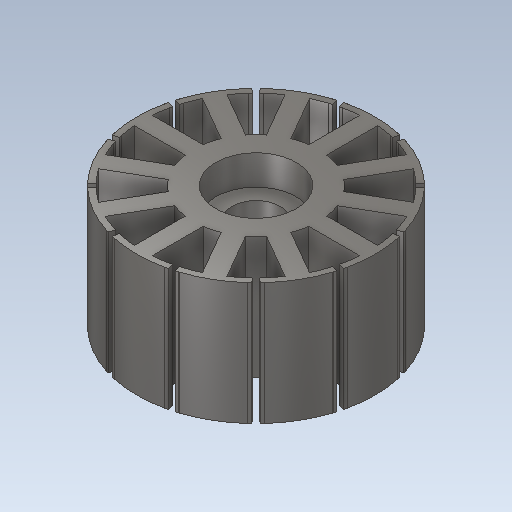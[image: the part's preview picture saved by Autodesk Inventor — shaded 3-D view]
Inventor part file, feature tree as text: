
AUTODESK INVENTOR PART (.ipt)
format: ipt  version: 2020.1 (Build 241239000, 239)  size: 308,224 bytes
history: native  units: mm
features: plane x1
ambient origin geometry x8: Origin, YZ Plane, XZ Plane, XY Plane, X Axis, Y Axis, Z Axis, Center Point
bodies: Solid1 (feature_tree), Body1 (feature_tree)
feature tree (1):
  plane  "Work Plane1"
